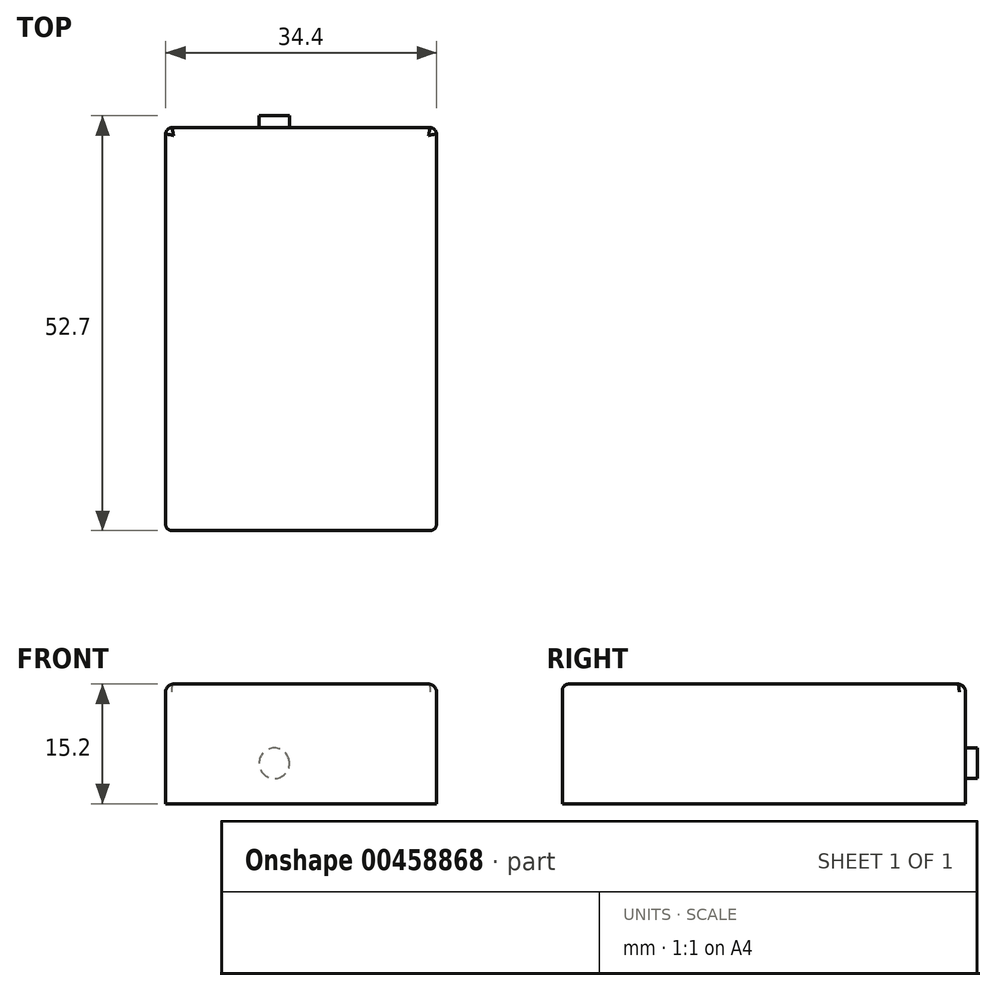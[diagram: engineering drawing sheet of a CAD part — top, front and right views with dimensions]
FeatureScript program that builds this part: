
annotation { "Feature Type Name" : "Feature", "Feature Type Description" : "" }
export const myFeature = defineFeature(function(context is Context, id is Id, definition is map)
    precondition{}
    {
        {
            var Q0;
            Q0=qCreatedBy(makeId("Front.planeOp"),FACE);
            var sketch = newSketch(context, id + "F0", { "sketchPlane" : qUnion([Q0])});
            skLineSegment(sketch, "E0.bottom", {"start": v(0, 0) * mm, "end": v(34.4, 0) * mm});
            skLineSegment(sketch, "E0.top", {"start": v(0, 15.2) * mm, "end": v(34.4, 15.2) * mm});
            skLineSegment(sketch, "E0.left", {"start": v(0, 0) * mm, "end": v(0, 15.2) * mm});
            skLineSegment(sketch, "E0.right", {"start": v(34.4, 0) * mm, "end": v(34.4, 15.2) * mm});
            skSolve(sketch);
        }
        {
            var Q0;
            Q0=makeQuery(id+"F0.imprint","IMPRINT",FACE,{"disambiguationData":[TD([[makeQuery(id+"F0.imprint","IMPRINT",EDGE,{"derivedFrom":sQuery(id+"F0.wireOp",EDGE,"E0.bottom")}),1.0]])]});
            extrude(context, id + "F1", {"entities" : qUnion([Q0]), "depth" : 51.2 * mm, "offsetDistance" : 25 * mm});
        }
        {
            var Q0;
            Q0=makeQuery(id+"F1.opExtrude","CAP_FACE",FACE,{"disambiguationData":[OSD([sQuery(id+"F0.wireOp",EDGE,"E0.bottom"),sQuery(id+"F0.wireOp",EDGE,"E0.top"),sQuery(id+"F0.wireOp",EDGE,"E0.left"),sQuery(id+"F0.wireOp",EDGE,"E0.right")])],"isStart":true});
            var sketch = newSketch(context, id + "F2", { "sketchPlane" : qUnion([Q0])});
            skCircle(sketch, "E1", {"center": v(-13.8, 5.15) * mm, "radius": 1.94 * mm});
            skSolve(sketch);
        }
        {
            var Q0;
            Q0=makeQuery(id+"F2.imprint","IMPRINT",FACE,{"disambiguationData":[TD([[makeQuery(id+"F2.imprint","IMPRINT",EDGE,{"derivedFrom":sQuery(id+"F2.wireOp",EDGE,"E1")}),1.0]])]});
            extrude(context, id + "F3", {"entities" : qUnion([Q0]), "operationType" : NewBodyOperationType.ADD, "depth" : 1.5 * mm, "offsetDistance" : 25 * mm});
        }
        {
            var Q0;
            Q0=makeQuery(id+"F1.opExtrude","SWEPT_EDGE",EDGE,{"disambiguationData":[OSD([sQuery(id+"F0.wireOp",EDGE,"E0.top"),sQuery(id+"F0.wireOp",EDGE,"E0.left")])]});
            var Q1;
            Q1=makeQuery(id+"F1.opExtrude","CAP_EDGE",EDGE,{"disambiguationData":[OSD([sQuery(id+"F0.wireOp",EDGE,"E0.top")])],"isStart":true});
            var Q2;
            Q2=makeQuery(id+"F1.opExtrude","SWEPT_EDGE",EDGE,{"disambiguationData":[OSD([sQuery(id+"F0.wireOp",EDGE,"E0.top"),sQuery(id+"F0.wireOp",EDGE,"E0.right")])]});
            fillet(context, id + "F4", {"entities" : qUnion([Q0, Q1, Q2]), "radius" : 1 * mm, "tangentPropagation" : true, "allowEdgeOverflow" : false});
        }
        {
            var Q0;
            Q0=makeQuery(id+"F1.opExtrude","CAP_EDGE",EDGE,{"disambiguationData":[OSD([sQuery(id+"F0.wireOp",EDGE,"E0.right")])],"isStart":true});
            var Q1;
            Q1=makeQuery(id+"F1.opExtrude","CAP_EDGE",EDGE,{"disambiguationData":[OSD([sQuery(id+"F0.wireOp",EDGE,"E0.left")])],"isStart":true});
            var Q2;
            Q2=makeQuery(id+"F1.opExtrude","CAP_EDGE",EDGE,{"disambiguationData":[OSD([sQuery(id+"F0.wireOp",EDGE,"E0.left")])],"isStart":false});
            fillet(context, id + "F5", {"entities" : qUnion([Q0, Q1, Q2]), "radius" : .8 * mm, "tangentPropagation" : true, "allowEdgeOverflow" : false});
        }
    });
